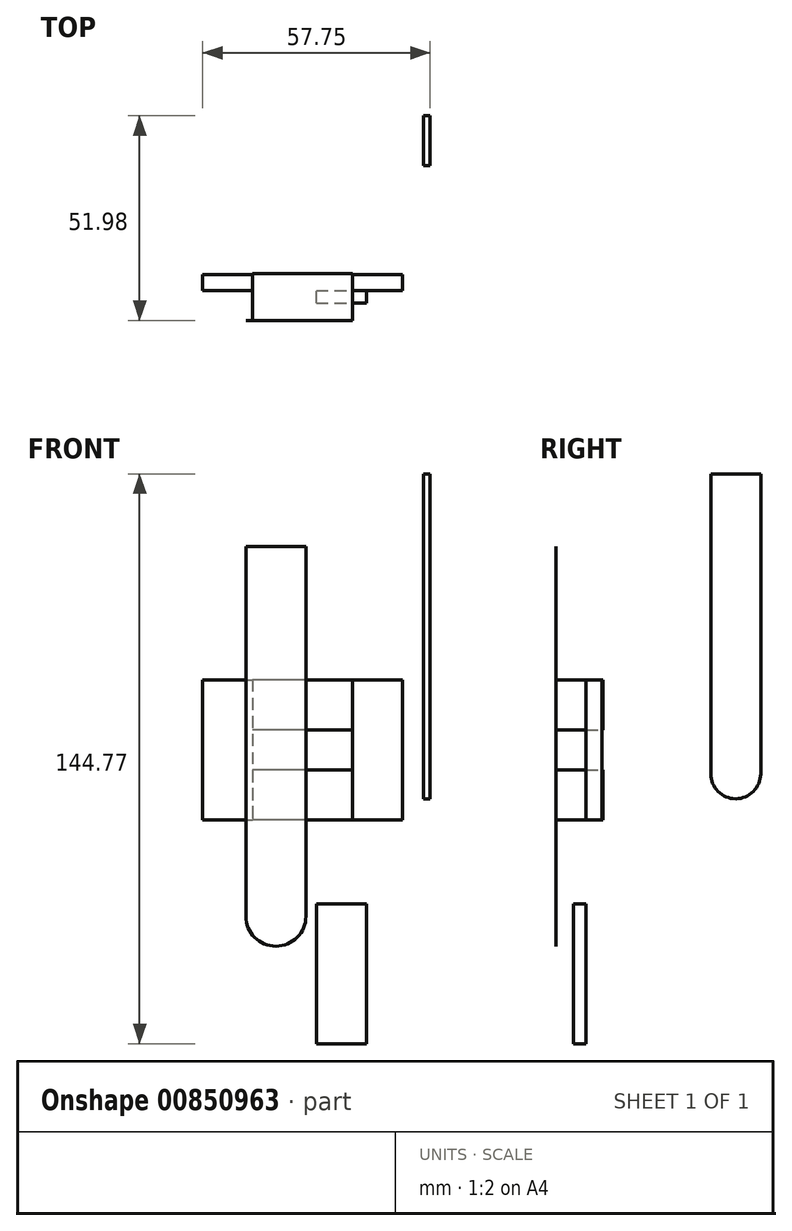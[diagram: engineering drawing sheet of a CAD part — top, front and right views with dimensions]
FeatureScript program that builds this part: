
annotation { "Feature Type Name" : "Feature", "Feature Type Description" : "" }
export const myFeature = defineFeature(function(context is Context, id is Id, definition is map)
    precondition{}
    {
        {
            var Q0;
            Q0=qCreatedBy(makeId("Front.planeOp"),FACE);
            var sketch = newSketch(context, id + "F0", { "sketchPlane" : qUnion([Q0])});
            skLineSegment(sketch, "E0.bottom", {"start": v(-56.1, 35.56) * mm, "end": v(-43.4, 35.56) * mm});
            skLineSegment(sketch, "E0.top", {"start": v(-56.1, 0) * mm, "end": v(-43.4, 0) * mm});
            skLineSegment(sketch, "E0.left", {"start": v(-56.1, 35.56) * mm, "end": v(-56.1, 0) * mm});
            skLineSegment(sketch, "E0.right", {"start": v(-43.4, 35.56) * mm, "end": v(-43.4, 0) * mm});
            skLineSegment(sketch, "E1.bottom", {"start": v(-18, 35.56) * mm, "end": v(-5.3, 35.56) * mm});
            skLineSegment(sketch, "E1.top", {"start": v(-18, 0) * mm, "end": v(-5.3, 0) * mm});
            skLineSegment(sketch, "E1.left", {"start": v(-18, 35.56) * mm, "end": v(-18, 0) * mm});
            skLineSegment(sketch, "E1.right", {"start": v(-5.3, 35.56) * mm, "end": v(-5.3, 0) * mm});
            skLineSegment(sketch, "E2.left", {"start": v(-18, 0) * mm, "end": v(-18, 0) * mm});
            skLineSegment(sketch, "E2.right", {"start": v(-43.4, 0) * mm, "end": v(-43.4, 0) * mm});
            skLineSegment(sketch, "E3.left", {"start": v(-43.4, 35.56) * mm, "end": v(-43.4, 35.56) * mm});
            skLineSegment(sketch, "E3.right", {"start": v(-18, 35.56) * mm, "end": v(-18, 35.56) * mm});
            skLineSegment(sketch, "E4.bottom", {"start": v(-5.3, 35.56) * mm, "end": v(-56.1, 35.56) * mm});
            skLineSegment(sketch, "E4.top", {"start": v(-5.3, 22.86) * mm, "end": v(-56.1, 22.86) * mm});
            skLineSegment(sketch, "E4.left", {"start": v(-5.3, 35.56) * mm, "end": v(-5.3, 22.86) * mm});
            skLineSegment(sketch, "E4.right", {"start": v(-56.1, 35.56) * mm, "end": v(-56.1, 22.86) * mm});
            skLineSegment(sketch, "E5.bottom", {"start": v(-5.3, 0) * mm, "end": v(-56.1, 0) * mm});
            skLineSegment(sketch, "E5.top", {"start": v(-5.3, 12.7) * mm, "end": v(-56.1, 12.7) * mm});
            skLineSegment(sketch, "E5.left", {"start": v(-5.3, 0) * mm, "end": v(-5.3, 12.7) * mm});
            skLineSegment(sketch, "E5.right", {"start": v(-56.1, 0) * mm, "end": v(-56.1, 12.7) * mm});
            skPoint(sketch, "E6", {"position": v(-43.4, 35.56) * mm});
            skPoint(sketch, "E7", {"position": v(-43.4, 22.86) * mm});
            skPoint(sketch, "E8", {"position": v(-18, 22.86) * mm});
            skPoint(sketch, "E9", {"position": v(-18, 12.7) * mm});
            skPoint(sketch, "E10", {"position": v(-43.4, 12.7) * mm});
            skSolve(sketch);
        }
        {
            var Q0;
            {var subQ5=sQuery(id+"F0.wireOp",EDGE,"E4.left");Q0=makeQuery(id+"F0.imprint","IMPRINT",FACE,{"disambiguationData":[TD([[makeQuery(id+"F0.imprint","IMPRINT",EDGE,{"derivedFrom":subQ5}),-1.0]])]});}
            var Q1;
            {var subQ0=sQuery(id+"F0.wireOp",EDGE,"E4.bottom");var subQ1=sQuery(id+"F0.wireOp",EDGE,"E0.right");var subQ2=makeQuery(id+"F0.imprint","INTERSECT",VERTEX,{"derivedFrom":[subQ1,subQ0]});Q1=makeQuery(id+"F0.imprint","IMPRINT",FACE,{"disambiguationData":[TD([[makeQuery(id+"F0.imprint","IMPRINT",EDGE,{"disambiguationData":[TD([[subQ2,-1.0]])],"derivedFrom":subQ1}),1.0]])]});}
            var Q2;
            {var subQ5=sQuery(id+"F0.wireOp",EDGE,"E4.right");Q2=makeQuery(id+"F0.imprint","IMPRINT",FACE,{"disambiguationData":[TD([[makeQuery(id+"F0.imprint","IMPRINT",EDGE,{"derivedFrom":subQ5}),1.0]])]});}
            var Q3;
            {var subQ5=sQuery(id+"F0.wireOp",EDGE,"E5.right");Q3=makeQuery(id+"F0.imprint","IMPRINT",FACE,{"disambiguationData":[TD([[makeQuery(id+"F0.imprint","IMPRINT",EDGE,{"derivedFrom":subQ5}),-1.0]])]});}
            var Q4;
            {var subQ0=sQuery(id+"F0.wireOp",EDGE,"E5.bottom");var subQ1=sQuery(id+"F0.wireOp",EDGE,"E0.right");var subQ2=makeQuery(id+"F0.imprint","INTERSECT",VERTEX,{"derivedFrom":[subQ1,subQ0]});Q4=makeQuery(id+"F0.imprint","IMPRINT",FACE,{"disambiguationData":[TD([[makeQuery(id+"F0.imprint","IMPRINT",EDGE,{"disambiguationData":[TD([[subQ2,1.0]])],"derivedFrom":subQ1}),1.0]])]});}
            var Q5;
            {var subQ5=sQuery(id+"F0.wireOp",EDGE,"E5.left");Q5=makeQuery(id+"F0.imprint","IMPRINT",FACE,{"disambiguationData":[TD([[makeQuery(id+"F0.imprint","IMPRINT",EDGE,{"derivedFrom":subQ5}),1.0]])]});}
            extrude(context, id + "F1", {"entities" : qUnion([Q0, Q1, Q2, Q3, Q4, Q5]), "depth" : 7.62 * mm, "offsetDistance" : 25.4 * mm, "hasSecondDirection" : true, "secondDirectionOppositeDirection" : true, "secondDirectionDepth" : 4.32 * mm});
        }
        {
            var Q0;
            {var subQ5=sQuery(id+"F0.wireOp",EDGE,"E1.right");Q0=makeQuery(id+"F0.imprint","IMPRINT",FACE,{"disambiguationData":[TD([[makeQuery(id+"F0.imprint","IMPRINT",EDGE,{"derivedFrom":subQ5}),-1.0]])]});}
            var Q1;
            {var subQ0=sQuery(id+"F0.wireOp",EDGE,"E0.left");Q1=makeQuery(id+"F0.imprint","IMPRINT",FACE,{"disambiguationData":[TD([[makeQuery(id+"F0.imprint","IMPRINT",EDGE,{"derivedFrom":subQ0}),1.0]])]});}
            extrude(context, id + "F2", {"entities" : qUnion([Q0, Q1]), "oppositeDirection" : true, "depth" : 4.06 * mm, "offsetDistance" : 25.4 * mm});
        }
        {
            var Q0;
            Q0=makeQuery(id+"F1.opExtrude","CAP_FACE",FACE,{"disambiguationData":[OSD([sQuery(id+"F0.wireOp",EDGE,"E5.bottom"),sQuery(id+"F0.wireOp",EDGE,"E5.top"),sQuery(id+"F0.wireOp",EDGE,"E5.left"),sQuery(id+"F0.wireOp",EDGE,"E5.right")])],"isStart":false});
            var sketch = newSketch(context, id + "F3", { "sketchPlane" : qUnion([Q0])});
            skLineSegment(sketch, "E11.right", {"start": v(-29.9, -24.5) * mm, "end": v(-29.9, 69.49) * mm});
            skLineSegment(sketch, "E12.2.0.0", {"start": v(-45.14, -24.5) * mm, "end": v(-45.14, 69.49) * mm});
            skArc(sketch, "E13", {"start": v(-45.14, -24.5) * mm, "mid": v(-37.52, -32.11) * mm, "end": v(-29.9, -24.5) * mm});
            skLineSegment(sketch, "E14", {"start": v(-45.14, 69.49) * mm, "end": v(-29.9, 69.49) * mm});
            skLineSegment(sketch, "E15.top", {"start": v(-25.15, 69.63) * mm, "end": v(-9.91, 69.63) * mm});
            skLineSegment(sketch, "E15.left", {"start": v(-25.15, -24.35) * mm, "end": v(-25.15, 69.63) * mm});
            skLineSegment(sketch, "E15.right", {"start": v(-9.91, -24.35) * mm, "end": v(-9.91, 69.63) * mm});
            skArc(sketch, "E16", {"start": v(-25.15, -24.35) * mm, "mid": v(-17.53, -31.97) * mm, "end": v(-9.91, -24.35) * mm});
            skSolve(sketch);
        }
        {
            var Q0;
            {var subQ0=sQuery(id+"F3.wireOp",EDGE,"zkDOKMRj-cckF-f1Yj-jk90-TssuszAsvcqZ");Q0=makeQuery(id+"F3.imprint","IMPRINT",FACE,{"disambiguationData":[TD([[makeQuery(id+"F3.imprint","IMPRINT",EDGE,{"derivedFrom":subQ0}),1.0]])]});}
            var Q1;
            {var subQ0=sQuery(id+"F3.wireOp",EDGE,"E13");Q1=makeQuery(id+"F3.imprint","IMPRINT",FACE,{"disambiguationData":[TD([[makeQuery(id+"F3.imprint","IMPRINT",EDGE,{"derivedFrom":subQ0}),1.0]])]});}
            var Q2;
            {var subQ0=sQuery(id+"F3.wireOp",EDGE,"E11.left");var subQ1=makeQuery(id+"F1.opExtrude","CAP_EDGE",EDGE,{"disambiguationData":[OSD([sQuery(id+"F0.wireOp",EDGE,"E5.bottom")])],"isStart":false});var subQ2=makeQuery(id+"F3.imprint","INTERSECT",VERTEX,{"derivedFrom":[subQ1,subQ0]});Q2=makeQuery(id+"F3.imprint","IMPRINT",FACE,{"disambiguationData":[TD([[makeQuery(id+"F3.imprint","IMPRINT",EDGE,{"disambiguationData":[TD([[subQ2,-1.0]])],"derivedFrom":subQ0}),1.0]])]});}
            var Q3;
            {var subQ0=sQuery(id+"F3.wireOp",EDGE,"E11.right");var subQ1=makeQuery(id+"F1.opExtrude","CAP_EDGE",EDGE,{"disambiguationData":[OSD([sQuery(id+"F0.wireOp",EDGE,"E5.bottom")])],"isStart":false});var subQ2=makeQuery(id+"F3.imprint","INTERSECT",VERTEX,{"derivedFrom":[subQ1,subQ0]});Q3=makeQuery(id+"F3.imprint","IMPRINT",FACE,{"disambiguationData":[TD([[makeQuery(id+"F3.imprint","IMPRINT",EDGE,{"disambiguationData":[TD([[subQ2,-1.0]])],"derivedFrom":subQ0}),1.0]])]});}
            var Q4;
            {var subQ0=sQuery(id+"F3.wireOp",EDGE,"E11.top");Q4=makeQuery(id+"F3.imprint","IMPRINT",FACE,{"disambiguationData":[TD([[makeQuery(id+"F3.imprint","IMPRINT",EDGE,{"derivedFrom":subQ0}),1.0]])]});}
            var Q5;
            {var subQ0=sQuery(id+"F3.wireOp",EDGE,"E14");Q5=makeQuery(id+"F3.imprint","IMPRINT",FACE,{"disambiguationData":[TD([[makeQuery(id+"F3.imprint","IMPRINT",EDGE,{"derivedFrom":subQ0}),-1.0]])]});}
            extrude(context, id + "F4", {"entities" : qUnion([Q0, Q1, Q2, Q3, Q4, Q5]), "depth" : 1 / 203.2 * mm, "offsetDistance" : 25.4 * mm});
        }
        {
            var Q0;
            Q0=qCreatedBy(makeId("Right.planeOp"),FACE);
            var sketch = newSketch(context, id + "F5", { "sketchPlane" : qUnion([Q0])});
            skLineSegment(sketch, "E17.top", {"start": v(31.66, 87.9) * mm, "end": v(44.36, 87.9) * mm});
            skLineSegment(sketch, "E17.left", {"start": v(31.66, 11.7) * mm, "end": v(31.66, 87.9) * mm});
            skLineSegment(sketch, "E17.right", {"start": v(44.36, 11.7) * mm, "end": v(44.36, 87.9) * mm});
            skArc(sketch, "E18", {"start": v(31.66, 11.7) * mm, "mid": v(38.01, 5.35) * mm, "end": v(44.36, 11.7) * mm});
            skSolve(sketch);
        }
        {
            var Q0;
            Q0=makeQuery(id+"F5.imprint","IMPRINT",FACE,{"disambiguationData":[TD([[makeQuery(id+"F5.imprint","IMPRINT",EDGE,{"derivedFrom":sQuery(id+"F5.wireOp",EDGE,"E17.top")}),-1.0]])]});
            extrude(context, id + "F6", {"entities" : qUnion([Q0]), "depth" : 1.65 * mm, "offsetDistance" : 25.4 * mm});
        }
        {
            var Q0;
            Q0=qCreatedBy(makeId("Front.planeOp"),FACE);
            var sketch = newSketch(context, id + "F7", { "sketchPlane" : qUnion([Q0])});
            skLineSegment(sketch, "E19.bottom", {"start": v(-27.23, -56.87) * mm, "end": v(-14.53, -56.87) * mm});
            skLineSegment(sketch, "E19.top", {"start": v(-27.23, -21.31) * mm, "end": v(-14.53, -21.31) * mm});
            skLineSegment(sketch, "E19.left", {"start": v(-27.23, -56.87) * mm, "end": v(-27.23, -21.31) * mm});
            skLineSegment(sketch, "E19.right", {"start": v(-14.53, -56.87) * mm, "end": v(-14.53, -21.31) * mm});
            skSolve(sketch);
        }
        {
            var Q0;
            Q0 = qSketchRegion(id + "F7", true);
            extrude(context, id + "F8", {"entities" : qUnion([Q0]), "depth" : 3.17 * mm, "offsetDistance" : 25.4 * mm});
        }
    });
